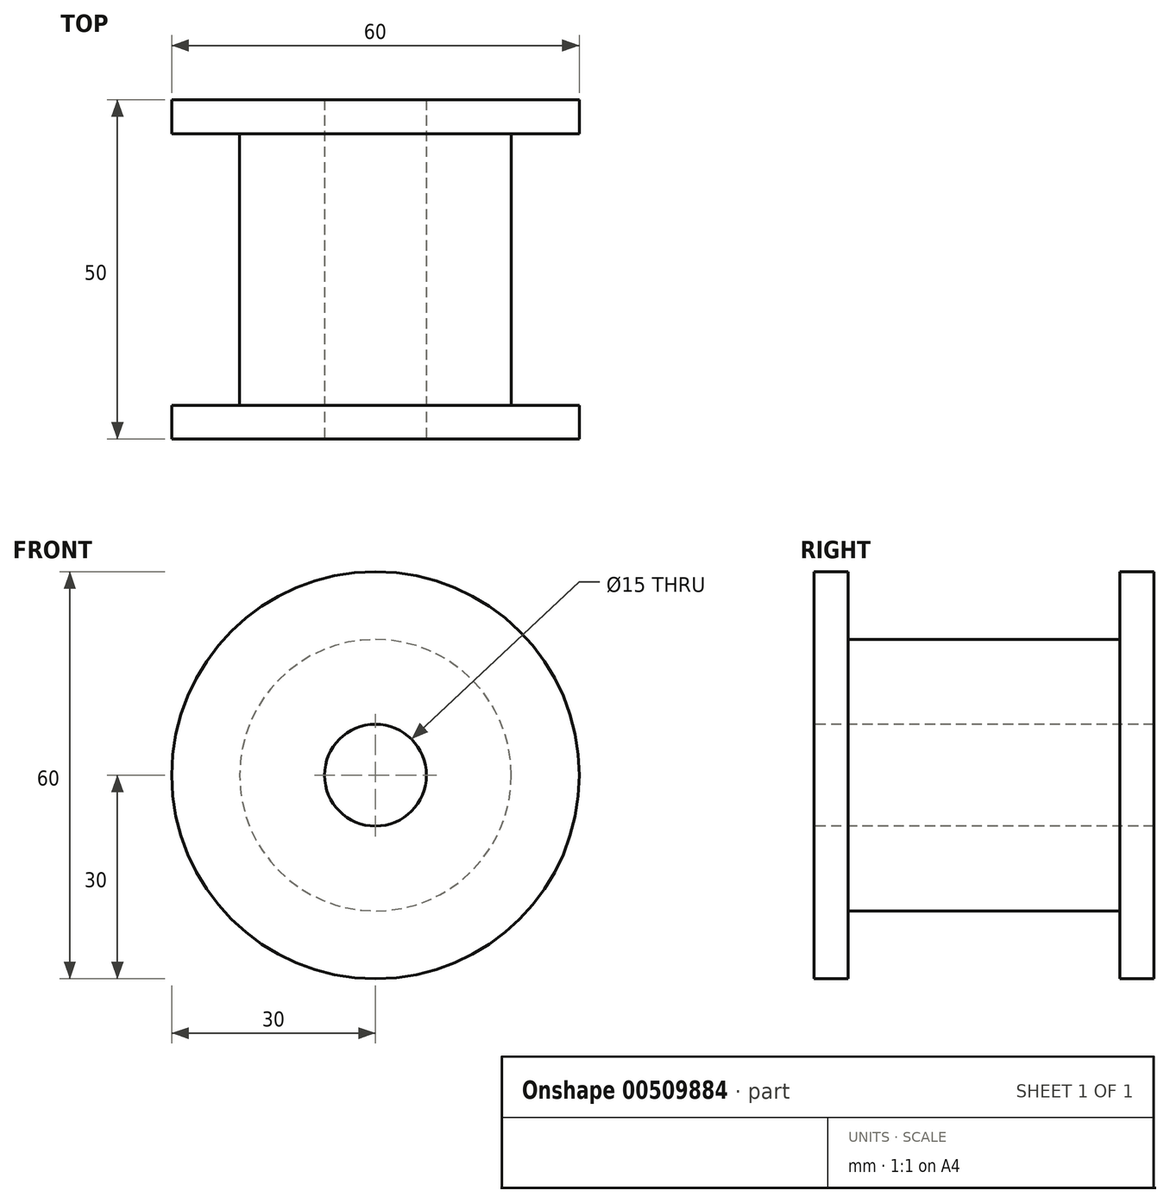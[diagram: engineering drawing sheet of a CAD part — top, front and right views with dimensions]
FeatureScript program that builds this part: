
annotation { "Feature Type Name" : "Feature", "Feature Type Description" : "" }
export const myFeature = defineFeature(function(context is Context, id is Id, definition is map)
    precondition{}
    {
        {
            var Q0;
            Q0=qCreatedBy(makeId("Right.planeOp"),FACE);
            var sketch = newSketch(context, id + "F0", { "sketchPlane" : qUnion([Q0])});
            skLineSegment(sketch, "E0", {"start": v(-25, 0) * mm, "end": v(-25, 30) * mm});
            skLineSegment(sketch, "E1", {"start": v(-25, 30) * mm, "end": v(-20, 30) * mm});
            skLineSegment(sketch, "E2", {"start": v(-20, 30) * mm, "end": v(-20, 20) * mm});
            skLineSegment(sketch, "E3", {"start": v(-20, 20) * mm, "end": v(20, 20) * mm});
            skLineSegment(sketch, "E4", {"start": v(20, 20) * mm, "end": v(20, 30) * mm});
            skLineSegment(sketch, "E5", {"start": v(20, 30) * mm, "end": v(25, 30) * mm});
            skLineSegment(sketch, "E6", {"start": v(25, 30) * mm, "end": v(25, 0) * mm});
            skLineSegment(sketch, "E7", {"start": v(-25, 0) * mm, "end": v(25, 0) * mm});
            skSolve(sketch);
        }
        {
            var Q0;
            Q0=makeQuery(id+"F0.imprint","IMPRINT",FACE,{"disambiguationData":[TD([[makeQuery(id+"F0.imprint","IMPRINT",EDGE,{"derivedFrom":sQuery(id+"F0.wireOp",EDGE,"E0")}),-1.0]])]});
            var Q1;
            Q1=sQuery(id+"F0.wireOp",EDGE,"E7");
            revolve(context, id + "F1", {"entities" : qUnion([Q0]), "axis" : qUnion([Q1]), "revolveType" : RevolveType.SYMMETRIC, "angle" : 360 * degree});
        }
        {
            var Q0;
            Q0=makeQuery(id+"F1.opRevolve","SWEPT_FACE",FACE,{"disambiguationData":[OSD([sQuery(id+"F0.wireOp",EDGE,"E0")])]});
            var sketch = newSketch(context, id + "F2", { "sketchPlane" : qUnion([Q0])});
            skCircle(sketch, "E8", {"center": v(0, 0) * mm, "radius": 7.5 * mm});
            skSolve(sketch);
        }
        {
            var Q0;
            Q0=sQuery(id+"F2.wireOp",VERTEX,"E8.center");
            var Q1;
            Q1=makeQuery(id+"F1.opRevolve","SWEPT_BODY",BODY,{"disambiguationData":[OSD([sQuery(id+"F0.wireOp",EDGE,"E0"),sQuery(id+"F0.wireOp",EDGE,"E1"),sQuery(id+"F0.wireOp",EDGE,"E2"),sQuery(id+"F0.wireOp",EDGE,"E3"),sQuery(id+"F0.wireOp",EDGE,"E4"),sQuery(id+"F0.wireOp",EDGE,"E5"),sQuery(id+"F0.wireOp",EDGE,"E6"),sQuery(id+"F0.wireOp",EDGE,"E7")])]});
            hole(context, id + "F3", {"style" : HoleStyle.SIMPLE, "endStyle" : HoleEndStyle.THROUGH, "holeDiameter" : 15 * mm, "isTappedThrough" : true, "tappedDepth" : 12 * mm, "tapClearance" : 3, "locations" : qUnion([Q0]), "scope" : qUnion([Q1])});
        }
    });
